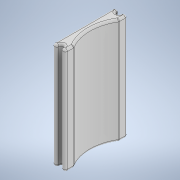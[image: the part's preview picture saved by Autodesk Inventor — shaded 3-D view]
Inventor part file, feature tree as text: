
AUTODESK INVENTOR PART (.ipt)
format: ipt  version: 2020 (Build 240168000, 168)  size: 180,736 bytes
history: native  units: in
note: dims shown in document units (in); Inventor stores cm internally (conversion verified against a paired STEP export)
features: fillet x2, extrude x1, sketch x1
ambient origin geometry x8: Origin, YZ Plane, XZ Plane, XY Plane, X Axis, Y Axis, Z Axis, Center Point
bodies: Solid1 (feature_tree)
feature tree (4):
  extrude  "Extrusion1"  Depth=0.0787in
  fillet  "Fillet1"  Radius=0.0787in
  fillet  "Fillet2"  Radius=0.2362in
  sketch  "Sketch1"  dims[d0=0.994in d1=0.0787in d2=0.0787in d3=0.2362in d4=0.0787in d5=0.0787in d6=0.0787in d7=0.0787in d8=0.0787in d9=0.2362in d10=0.0787in d11=0.0787in d12=0.0787in d13=1.9685in d14=0.0in d15=0.0394in d16=0.0394in]
